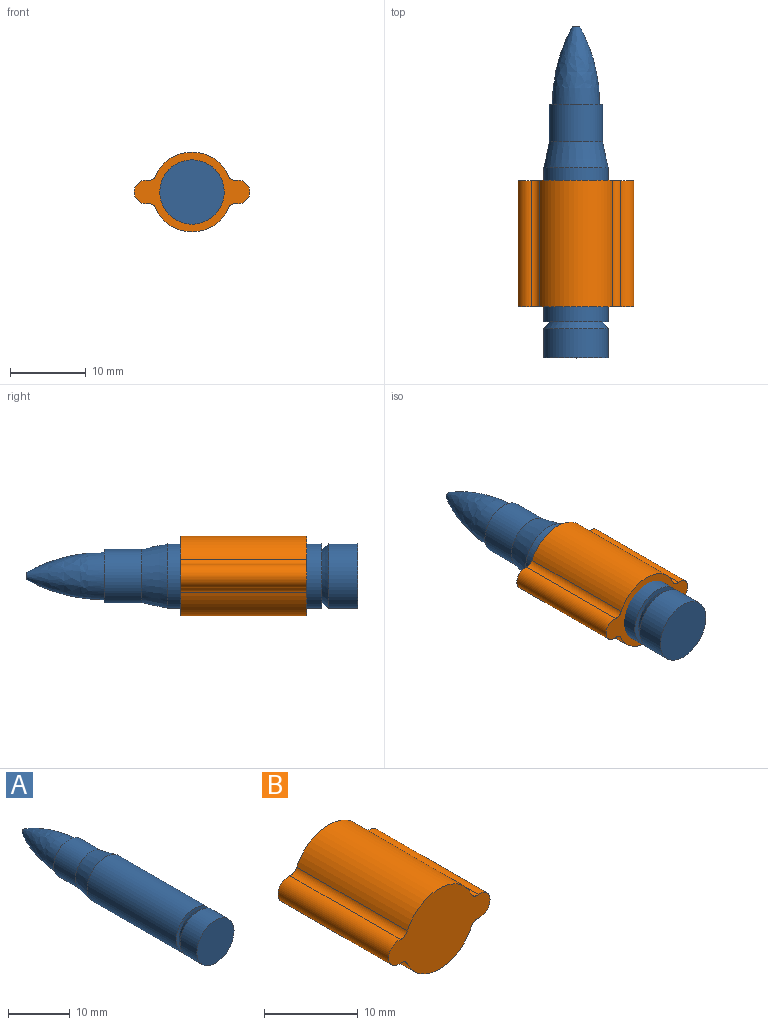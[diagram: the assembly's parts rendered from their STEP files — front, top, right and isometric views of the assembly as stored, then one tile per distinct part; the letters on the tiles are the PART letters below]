
ASSEMBLY  parts=2 mates=1
PART A: 10 faces, bbox 8.5x43.9x8.5 mm
  f0: plane 7.08x7.08mm, normal (0,1,0), area 8.4mm2, adj f1,f9
  f1: revolved ~10.36x6.28mm, area 151.9mm2, adj f0,f2
  f2: plane 0.88x0.88mm, normal (0,1,0), area 0.6mm2, adj f1
  f3: plane 8.51x8.51mm, normal (0,-1,0), area 56.9mm2, adj f4
  f4: cylinder r=4.26mm len=8.51mm, axis (0,-1,0), area 103mm2, adj f3,f5
  f5: cone r=3.54mm half-angle=37.7deg, axis (0,-1,0), area 28.7mm2, adj f4,f6
  f6: plane 8.51x8.51mm, normal (0,-1,0), area 17.5mm2, adj f5,f7
  f7: cylinder r=4.26mm len=20.42mm, axis (0,-1,0), area 546mm2, adj f6,f8
  f8: cone r=4.26mm half-angle=11.9deg, axis (0,-1,0), area 85mm2, adj f7,f9
  f9: cylinder r=3.54mm len=7.08mm, axis (0,-1,0), area 110.7mm2, adj f0,f8
PART B: 10 faces, bbox 15.3x16.7x10.6 mm
  f0: cylinder r=5.28mm len=16.7mm, axis (0,-1,0), area 203.3mm2, adj f3,f4,f6,f9
  f1: cylinder r=1.57mm len=16.7mm, axis (0,-1,0), area 89.6mm2, adj f3,f4,f5,f6
  f2: cylinder r=5.28mm len=16.7mm, axis (0,-1,0), area 203.3mm2, adj f3,f4,f5,f8
  f3: plane 15.32x10.55mm, normal (0,1,0), area 101.1mm2, adj f0,f1,f2,f5,f6,f7,f8,f9
  f4: plane 15.32x10.55mm, normal (0,-1,0), area 101.1mm2, adj f0,f1,f2,f5,f6,f7,f8,f9
  f5: cylinder r=1mm len=16.7mm, axis (0,1,0), area 21.6mm2, adj f1,f2,f3,f4
  f6: cylinder r=1mm len=16.7mm, axis (0,1,0), area 21.6mm2, adj f0,f1,f3,f4
  f7: cylinder r=1.57mm len=16.7mm, axis (0,-1,0), area 89.6mm2, adj f3,f4,f8,f9
  f8: cylinder r=1mm len=16.7mm, axis (0,1,0), area 21.6mm2, adj f2,f3,f4,f7
  f9: cylinder r=1mm len=16.7mm, axis (0,1,0), area 21.6mm2, adj f0,f3,f4,f7
PLACE A t=(5.12,-8.27,5.86)mm
PLACE B t=(5.12,-6.89,5.86)mm
MATE fastened A.f4 <-> B.f0  axis (0,-1,0) through (5.12,-3.49,5.86)mm
